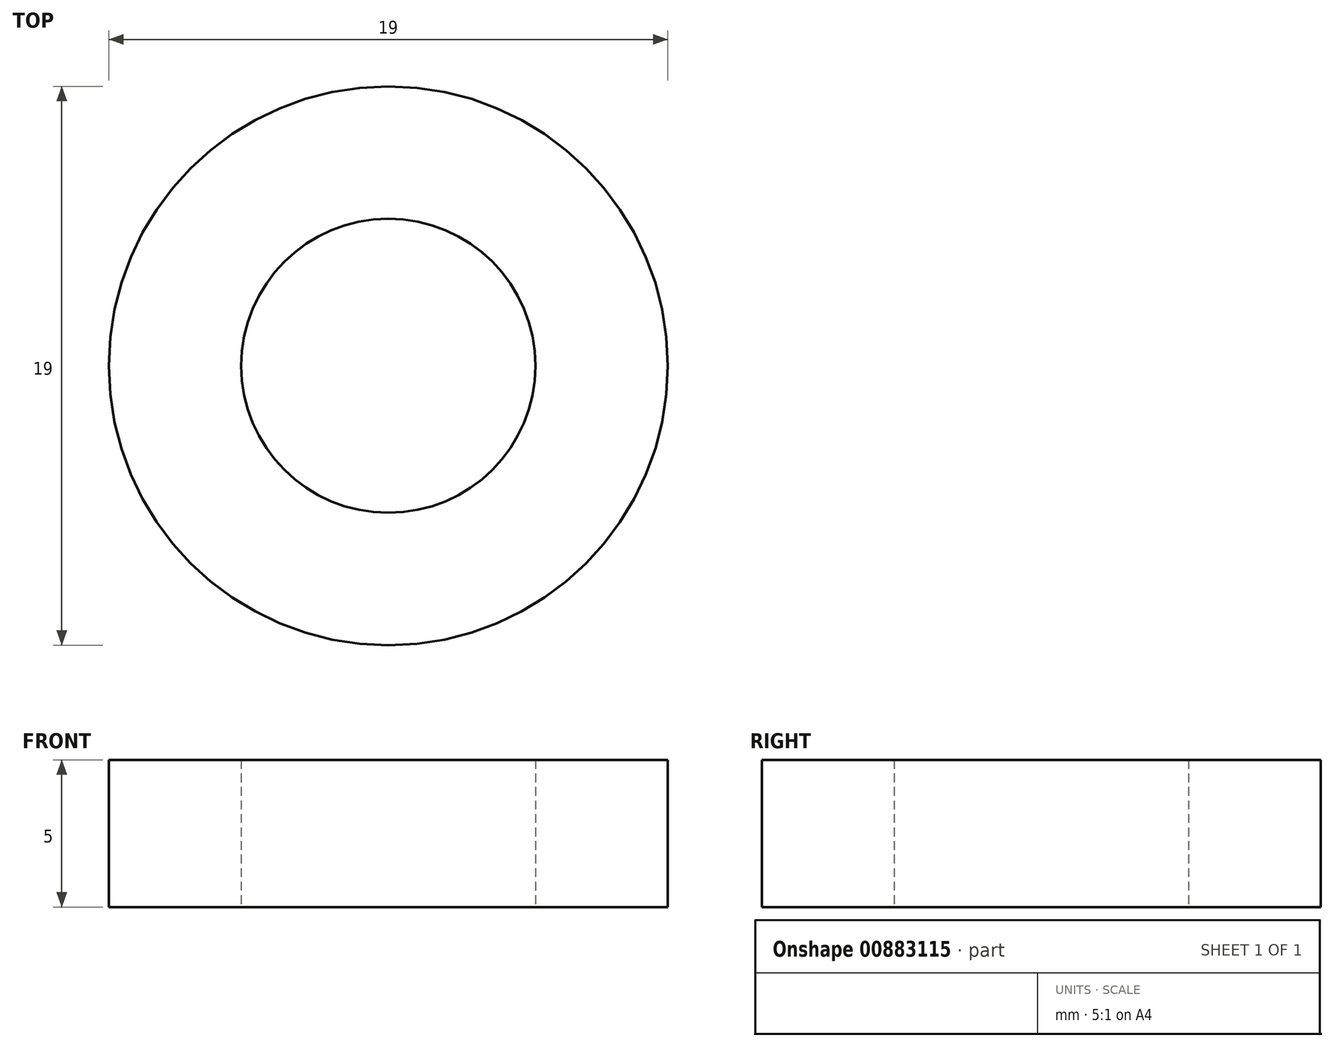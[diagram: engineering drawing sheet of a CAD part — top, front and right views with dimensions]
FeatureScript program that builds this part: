
annotation { "Feature Type Name" : "Feature", "Feature Type Description" : "" }
export const myFeature = defineFeature(function(context is Context, id is Id, definition is map)
    precondition{}
    {
        {
            var Q0;
            Q0=qCreatedBy(makeId("Top.planeOp"),FACE);
            var sketch = newSketch(context, id + "F0", { "sketchPlane" : qUnion([Q0])});
            skCircle(sketch, "E0", {"center": v(0, 0) * mm, "radius": 5 * mm});
            skCircle(sketch, "E1", {"center": v(0, 0) * mm, "radius": 9.5 * mm});
            skSolve(sketch);
        }
        {
            var Q0;
            Q0=makeQuery(id+"F0.imprint","IMPRINT",FACE,{"disambiguationData":[TD([[makeQuery(id+"F0.imprint","IMPRINT",EDGE,{"derivedFrom":sQuery(id+"F0.wireOp",EDGE,"E0")}),-1.0]])]});
            extrude(context, id + "F1", {"entities" : qUnion([Q0]), "depth" : 5 * mm, "offsetDistance" : 25 * mm});
        }
    });
